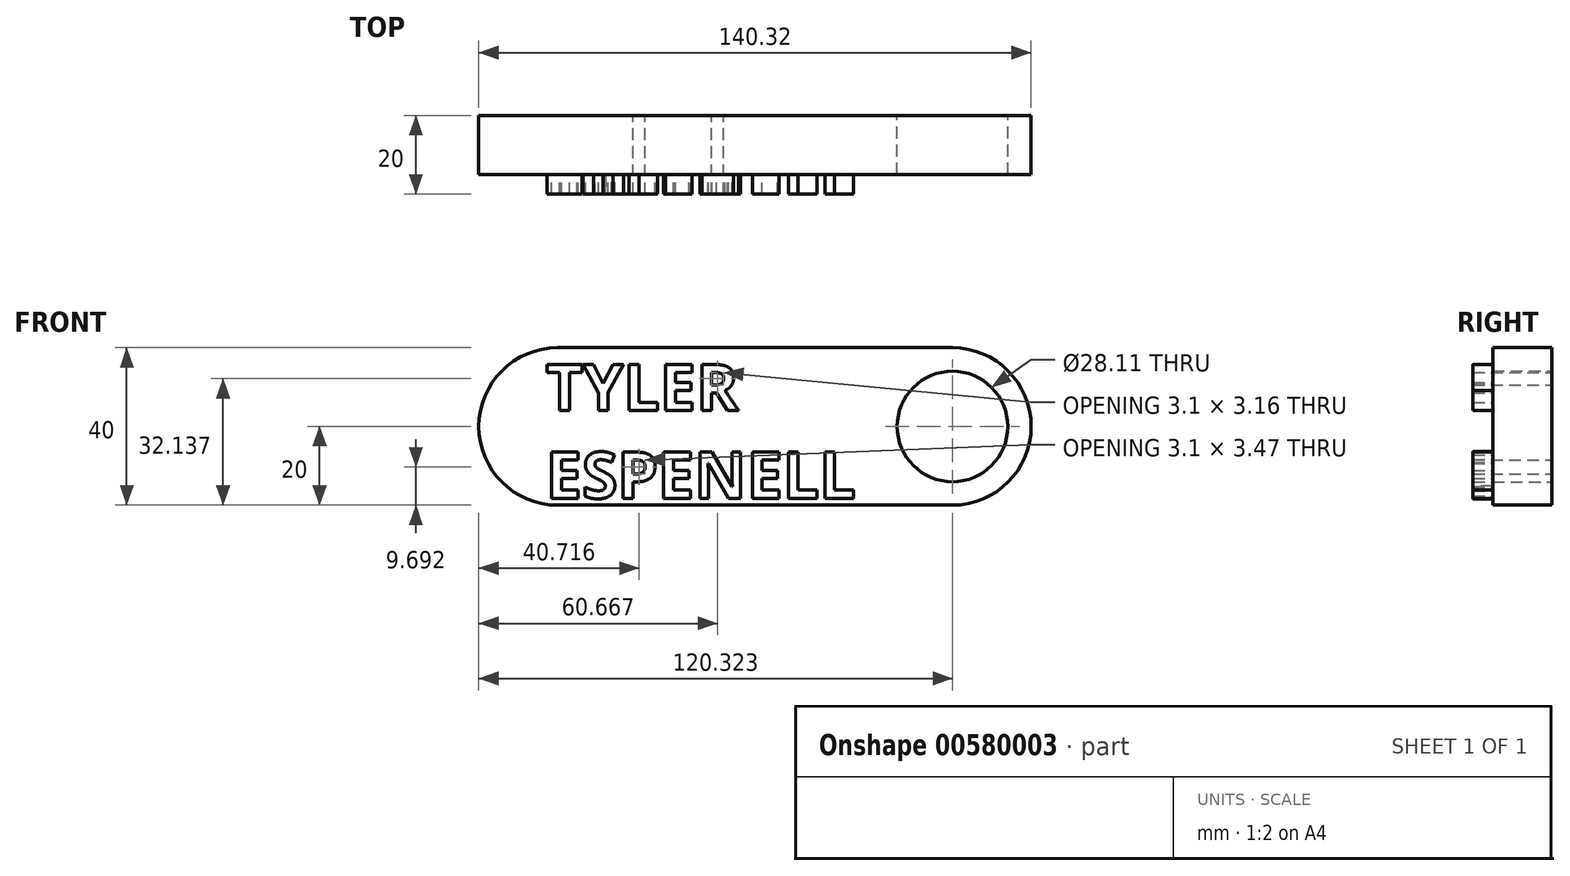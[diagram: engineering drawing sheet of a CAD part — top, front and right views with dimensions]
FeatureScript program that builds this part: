
annotation { "Feature Type Name" : "Feature", "Feature Type Description" : "" }
export const myFeature = defineFeature(function(context is Context, id is Id, definition is map)
    precondition{}
    {
        {
            var Q0;
            Q0=qCreatedBy(makeId("Front.planeOp"),FACE);
            var sketch = newSketch(context, id + "F0", { "sketchPlane" : qUnion([Q0])});
            skArc(sketch, "E0", {"start": v(-48.23, 20) * mm, "mid": v(-68.23, 0) * mm, "end": v(-48.23, -20) * mm});
            skArc(sketch, "E1", {"start": v(52.1, -20) * mm, "mid": v(72.1, 0) * mm, "end": v(52.1, 20) * mm});
            skLineSegment(sketch, "E2", {"start": v(-48.23, 20) * mm, "end": v(52.1, 20) * mm});
            skLineSegment(sketch, "E3", {"start": v(-48.23, -20) * mm, "end": v(52.1, -20) * mm});
            skText(sketch, "E4", { "text": "TYLER\nESPENELL", "fontName": "OpenSans-Bold.ttf"});
            skCircle(sketch, "E5", {"center": v(52.1, 0) * mm, "radius": 14.06 * mm});
            const initialGuessF0  = {"E4": [-0.05122, 0.00405, 1, 0, 0.0118]};
            skSetInitialGuess(sketch, initialGuessF0);
            skSolve(sketch);
        }
        {
            var Q0;
            Q0 = qSketchRegion(id + "F0", true);
            extrude(context, id + "F1", {"entities" : qUnion([Q0]), "depth" : 15 * mm, "offsetDistance" : 25 * mm});
        }
        {
            var Q0;
            Q0=makeQuery(id+"F0.imprint","IMPRINT",FACE,{"disambiguationData":[TD([[makeQuery(id+"F0.imprint","IMPRINT",EDGE,{"derivedFrom":sQuery(id+"F0.wireOp",EDGE,"E4.sketch_text.stroke-0")}),-1.0]])]});
            var Q1;
            Q1=makeQuery(id+"F0.imprint","IMPRINT",FACE,{"disambiguationData":[TD([[makeQuery(id+"F0.imprint","IMPRINT",EDGE,{"derivedFrom":sQuery(id+"F0.wireOp",EDGE,"E4.sketch_text.stroke-8")}),-1.0]])]});
            var Q2;
            Q2=makeQuery(id+"F0.imprint","IMPRINT",FACE,{"disambiguationData":[TD([[makeQuery(id+"F0.imprint","IMPRINT",EDGE,{"derivedFrom":sQuery(id+"F0.wireOp",EDGE,"E4.sketch_text.stroke-17")}),-1.0]])]});
            var Q3;
            Q3=makeQuery(id+"F0.imprint","IMPRINT",FACE,{"disambiguationData":[TD([[makeQuery(id+"F0.imprint","IMPRINT",EDGE,{"derivedFrom":sQuery(id+"F0.wireOp",EDGE,"E4.sketch_text.stroke-23")}),-1.0]])]});
            var Q4;
            Q4=makeQuery(id+"F0.imprint","IMPRINT",FACE,{"disambiguationData":[TD([[makeQuery(id+"F0.imprint","IMPRINT",EDGE,{"derivedFrom":sQuery(id+"F0.wireOp",EDGE,"E4.sketch_text.stroke-35")}),-1.0]])]});
            var Q5;
            Q5=makeQuery(id+"F0.imprint","IMPRINT",FACE,{"disambiguationData":[TD([[makeQuery(id+"F0.imprint","IMPRINT",EDGE,{"derivedFrom":sQuery(id+"F0.wireOp",EDGE,"E4.sketch_text.stroke-54")}),-1.0]])]});
            var Q6;
            Q6=makeQuery(id+"F0.imprint","IMPRINT",FACE,{"disambiguationData":[TD([[makeQuery(id+"F0.imprint","IMPRINT",EDGE,{"derivedFrom":sQuery(id+"F0.wireOp",EDGE,"E4.sketch_text.stroke-66")}),-1.0]])]});
            var Q7;
            Q7=makeQuery(id+"F0.imprint","IMPRINT",FACE,{"disambiguationData":[TD([[makeQuery(id+"F0.imprint","IMPRINT",EDGE,{"derivedFrom":sQuery(id+"F0.wireOp",EDGE,"E4.sketch_text.stroke-94")}),-1.0]])]});
            var Q8;
            Q8=makeQuery(id+"F0.imprint","IMPRINT",FACE,{"disambiguationData":[TD([[makeQuery(id+"F0.imprint","IMPRINT",EDGE,{"derivedFrom":sQuery(id+"F0.wireOp",EDGE,"E4.sketch_text.stroke-110")}),-1.0]])]});
            var Q9;
            Q9=makeQuery(id+"F0.imprint","IMPRINT",FACE,{"disambiguationData":[TD([[makeQuery(id+"F0.imprint","IMPRINT",EDGE,{"derivedFrom":sQuery(id+"F0.wireOp",EDGE,"E4.sketch_text.stroke-122")}),-1.0]])]});
            var Q10;
            Q10=makeQuery(id+"F0.imprint","IMPRINT",FACE,{"disambiguationData":[TD([[makeQuery(id+"F0.imprint","IMPRINT",EDGE,{"derivedFrom":sQuery(id+"F0.wireOp",EDGE,"E4.sketch_text.stroke-136")}),-1.0]])]});
            var Q11;
            Q11=makeQuery(id+"F0.imprint","IMPRINT",FACE,{"disambiguationData":[TD([[makeQuery(id+"F0.imprint","IMPRINT",EDGE,{"derivedFrom":sQuery(id+"F0.wireOp",EDGE,"E4.sketch_text.stroke-148")}),-1.0]])]});
            var Q12;
            Q12=makeQuery(id+"F0.imprint","IMPRINT",FACE,{"disambiguationData":[TD([[makeQuery(id+"F0.imprint","IMPRINT",EDGE,{"derivedFrom":sQuery(id+"F0.wireOp",EDGE,"E4.sketch_text.stroke-154")}),-1.0]])]});
            extrude(context, id + "F2", {"entities" : qUnion([Q0, Q1, Q2, Q3, Q4, Q5, Q6, Q7, Q8, Q9, Q10, Q11, Q12]), "operationType" : NewBodyOperationType.ADD, "depth" : 20 * mm, "offsetDistance" : 25 * mm});
        }
    });
